# Revit family: IS_TonicII_Multiproduct_BIM_DE_A6332;A6333
name_source: partatom
category: Plumbing Fixtures
revit_build: Autodesk Revit 2015 (Build: 20140606_1530(x64)
units: mm (PartAtom-declared; Revit-internal decimal feet)

## types (2) — shared parameters
A6332AA = Yes
AreaUnits = millimeters
Assembly Code = C1030200
AssetType = Fixed
Brand = Ideal Standard
ConnectionType = Plumbing
Default Elevation = 1219 mm
DurationUnit = year
ExpectedLife = 25
FaucetFunction = MIXED
FaucetOperation = Other
FaucetTopDescription = Lever
FaucetType = Other
Finish = Chrome
IfcExportAs = IfcValveType
IfcExportType = FAUCET
InstallationDate = 1900-12-31T23:59:59
InstallationInstructions = www.idealstandard.de\produkte
LinearUnits = millimeters
ManufacturerURL = www.idealstandard.com
NBSDescription = Water supply fitting for wash basins and troughs
NBSReference = 45-35-70/371
NominalDepth = 186 mm
NominalHeight = 175 mm
NominalLength = 186 mm
NominalWidth = 94 mm
ProductInformation = www.idealstandard.de/produkte
Shape = Sculptured
Size = 175 x 187 x 95 mm
Space = Internal
SpareParts = www.idealstandard.de/ersatzteile
TestPressure = 10 Bar
URL = www.idealstandard.com
Uniclass2015Code = Pr_40_20_87_98
Uniclass2015Title = Water supply fittings for wash basins and troughs
Uniclass2015Version = Products v1.1
Version = 1
VolumeUnits = Litres
WarrantyStartDate = 1900-12-31T23:59:59
WorkingPressure = 1-5 Bar

## per-type parameters (varying)
| type | BIMObjectName | BarCode | Description | Features | Model | ModelNumber | ModelReference | Name | NettWeight |
| A6332AA - | ISI_IdealStandard_WashBasinTaps_TonicII_A6332 | 4015413334990 | A6332AA TONIC II single lever one hole basin mixer, high spout, with pop-up waste | TONIC II single lever one hole basin mixer, high spout, with pop-up waste | A6332AA | A6332AA | Tonic ii single lever one hole high spout basin mixer with pop-up waste | WashBasinTaps_TonicII_A6332_IdealStandard | 1.9 Kg |
| A6333AA - | ISI_IdealStandard_WashBasinTaps_TonicII_A6333 | 4015413335003 | A6333AA TONIC II single lever one hole basin mixer, high spout, no pop-up waste | TONIC II single lever one hole basin mixer, high spout, no pop-up waste | A6333AA | A6333AA | Tonic ii single lever high spout basin mixer without pop-up waste | WashBasinTaps_TonicII_A6333_IdealStandard | 1.6 Kg |

## geometry (parser evidence)
native form markers: Blend x2, Sweep x3
no freeform markers — native parametric forms only
